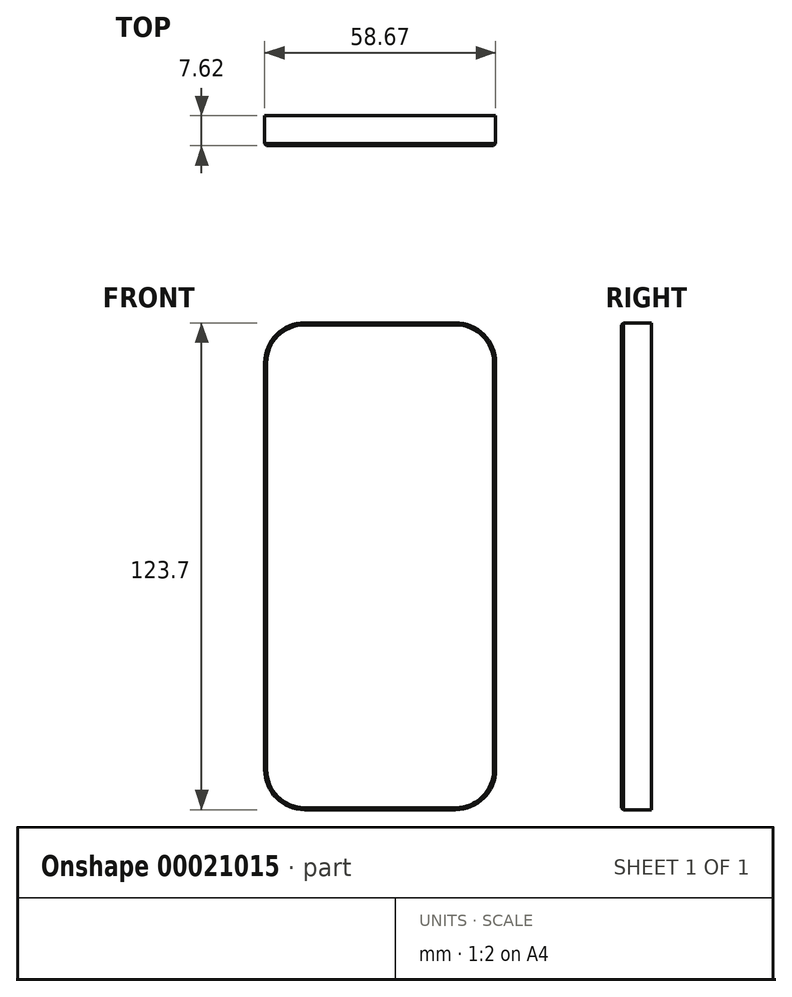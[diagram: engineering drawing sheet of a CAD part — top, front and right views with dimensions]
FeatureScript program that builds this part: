
annotation { "Feature Type Name" : "Feature", "Feature Type Description" : "" }
export const myFeature = defineFeature(function(context is Context, id is Id, definition is map)
    precondition{}
    {
        {
            var Q0;
            Q0=qCreatedBy(makeId("Front.planeOp"),FACE);
            var sketch = newSketch(context, id + "F0", { "sketchPlane" : qUnion([Q0])});
            skLineSegment(sketch, "E0.bottom", {"start": v(-42.16, 62.49) * mm, "end": v(16.51, 62.49) * mm});
            skLineSegment(sketch, "E0.top", {"start": v(-42.16, -61.2) * mm, "end": v(16.51, -61.2) * mm});
            skLineSegment(sketch, "E0.left", {"start": v(-42.16, 62.49) * mm, "end": v(-42.16, -61.2) * mm});
            skLineSegment(sketch, "E0.right", {"start": v(16.51, 62.49) * mm, "end": v(16.51, -61.2) * mm});
            skSolve(sketch);
        }
        {
            var Q0;
            Q0 = qSketchRegion(id + "F0", true);
            extrude(context, id + "F1", {"entities" : qUnion([Q0]), "depth" : 7.62 * mm});
        }
        {
            var Q0;
            Q0=makeQuery(id+"F1.opExtrude","SWEPT_EDGE",EDGE,{"disambiguationData":[OSD([sQuery(id+"F0.wireOp",EDGE,"E0.bottom"),sQuery(id+"F0.wireOp",EDGE,"E0.right")])]});
            var Q1;
            Q1=makeQuery(id+"F1.opExtrude","SWEPT_EDGE",EDGE,{"disambiguationData":[OSD([sQuery(id+"F0.wireOp",EDGE,"E0.bottom"),sQuery(id+"F0.wireOp",EDGE,"E0.left")])]});
            var Q2;
            Q2=makeQuery(id+"F1.opExtrude","SWEPT_EDGE",EDGE,{"disambiguationData":[OSD([sQuery(id+"F0.wireOp",EDGE,"E0.top"),sQuery(id+"F0.wireOp",EDGE,"E0.left")])]});
            var Q3;
            Q3=makeQuery(id+"F1.opExtrude","SWEPT_EDGE",EDGE,{"disambiguationData":[OSD([sQuery(id+"F0.wireOp",EDGE,"E0.top"),sQuery(id+"F0.wireOp",EDGE,"E0.right")])]});
            fillet(context, id + "F2", {"entities" : qUnion([Q0, Q1, Q2, Q3]), "radius" : 10.16 * mm, "tangentPropagation" : true, "allowEdgeOverflow" : false});
        }
        {
            var Q0;
            Q0=makeQuery(id+"F1.opExtrude","CAP_EDGE",EDGE,{"disambiguationData":[OSD([sQuery(id+"F0.wireOp",EDGE,"E0.right")])],"isStart":false});
            chamfer(context, id + "F3", {"entities" : qUnion([Q0]), "width" : 0.5 * mm, "tangentPropagation" : true});
        }
    });
